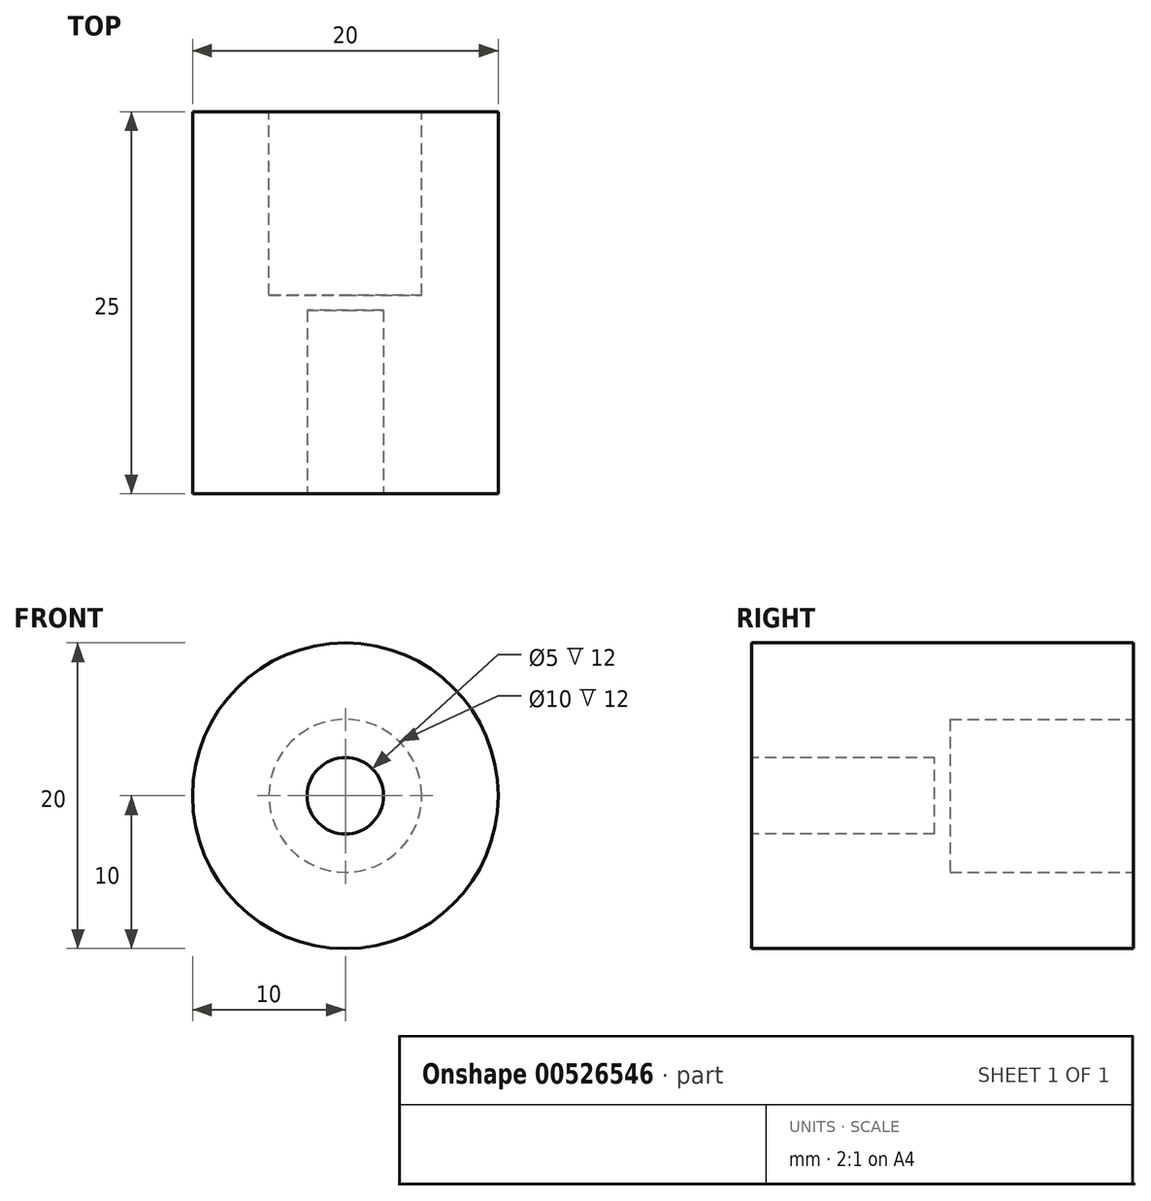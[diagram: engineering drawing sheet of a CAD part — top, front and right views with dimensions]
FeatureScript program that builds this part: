
annotation { "Feature Type Name" : "Feature", "Feature Type Description" : "" }
export const myFeature = defineFeature(function(context is Context, id is Id, definition is map)
    precondition{}
    {
        {
            var Q0;
            Q0=qCreatedBy(makeId("Front.planeOp"),FACE);
            var sketch = newSketch(context, id + "F0", { "sketchPlane" : qUnion([Q0])});
            skCircle(sketch, "E0", {"center": v(0, 0) * mm, "radius": 10 * mm});
            skSolve(sketch);
        }
        {
            var Q0;
            Q0=makeQuery(id+"F0.imprint","IMPRINT",FACE,{"disambiguationData":[TD([[makeQuery(id+"F0.imprint","IMPRINT",EDGE,{"derivedFrom":sQuery(id+"F0.wireOp",EDGE,"E0")}),1.0]])]});
            extrude(context, id + "F1", {"entities" : qUnion([Q0]), "endBound" : BoundingType.SYMMETRIC, "depth" : 25 * mm, "offsetDistance" : 25 * mm});
        }
        {
            var Q0;
            Q0=makeQuery(id+"F1.opExtrude","CAP_FACE",FACE,{"disambiguationData":[OSD([sQuery(id+"F0.wireOp",EDGE,"E0")])],"isStart":false});
            var sketch = newSketch(context, id + "F2", { "sketchPlane" : qUnion([Q0])});
            skCircle(sketch, "E1", {"center": v(0, 0) * mm, "radius": 2.5 * mm});
            skSolve(sketch);
        }
        {
            var Q0;
            Q0 = qSketchRegion(id + "F2", true);
            extrude(context, id + "F3", {"entities" : qUnion([Q0]), "operationType" : NewBodyOperationType.REMOVE, "oppositeDirection" : true, "depth" : 12 * mm, "offsetDistance" : 25 * mm});
        }
        {
            var Q0;
            Q0=makeQuery(id+"F1.opExtrude","CAP_FACE",FACE,{"disambiguationData":[OSD([sQuery(id+"F0.wireOp",EDGE,"E0")])],"isStart":true});
            var sketch = newSketch(context, id + "F4", { "sketchPlane" : qUnion([Q0])});
            skCircle(sketch, "E2", {"center": v(0, 0) * mm, "radius": 5 * mm});
            skSolve(sketch);
        }
        {
            var Q0;
            Q0 = qSketchRegion(id + "F4", true);
            extrude(context, id + "F5", {"entities" : qUnion([Q0]), "operationType" : NewBodyOperationType.REMOVE, "oppositeDirection" : true, "depth" : 12 * mm, "offsetDistance" : 25 * mm});
        }
    });
